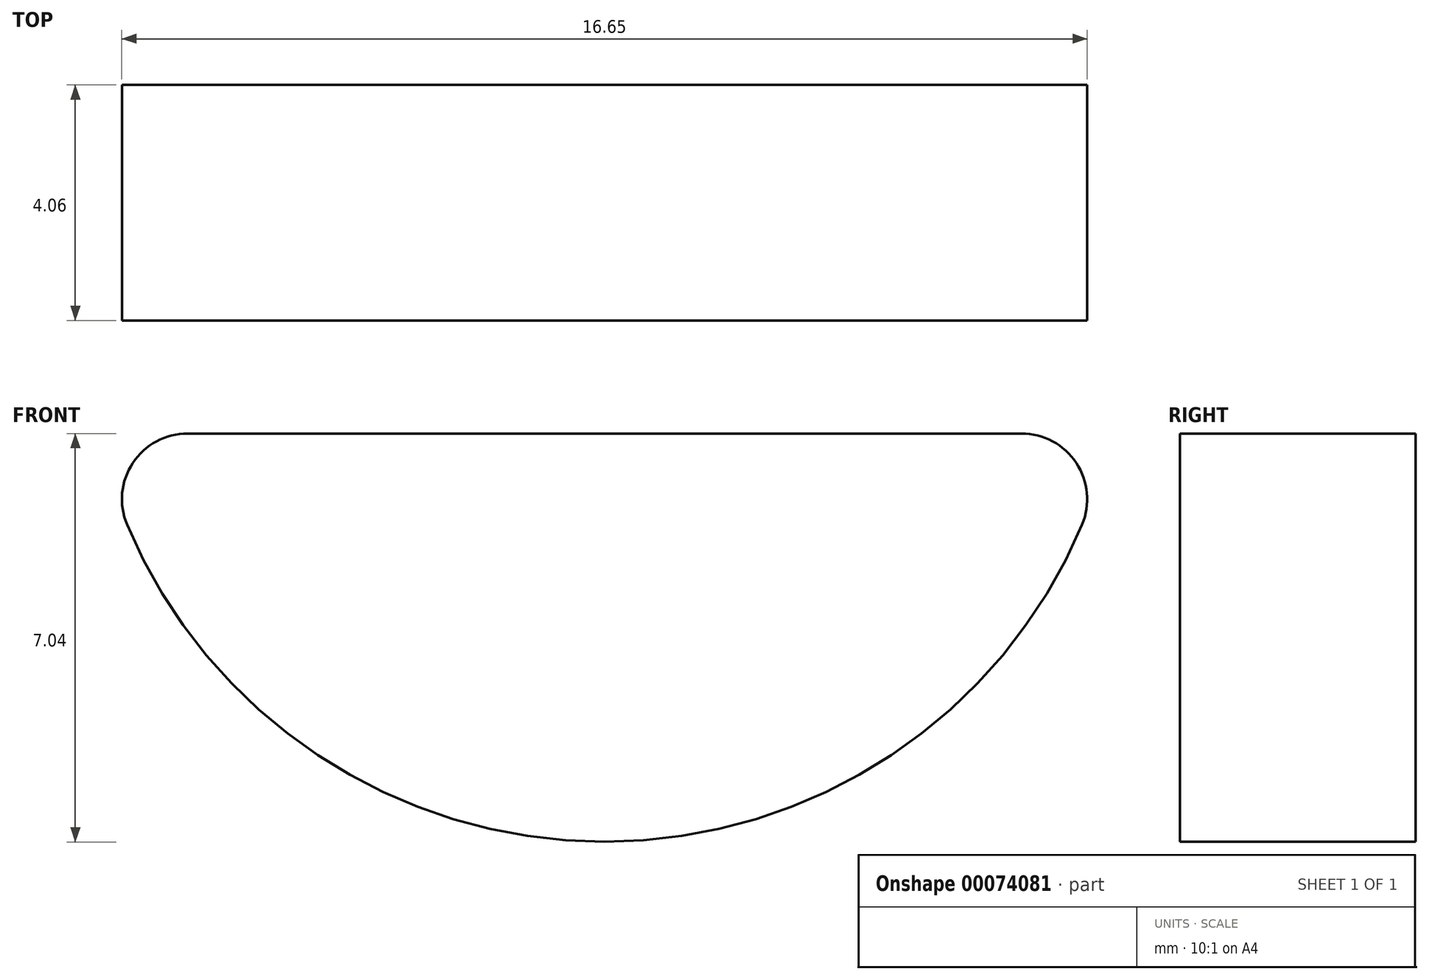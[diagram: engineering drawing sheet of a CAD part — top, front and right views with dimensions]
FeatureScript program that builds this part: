
annotation { "Feature Type Name" : "Feature", "Feature Type Description" : "" }
export const myFeature = defineFeature(function(context is Context, id is Id, definition is map)
    precondition{}
    {
        {
            var Q0;
            Q0=qCreatedBy(makeId("Front.planeOp"),FACE);
            var sketch = newSketch(context, id + "F0", { "sketchPlane" : qUnion([Q0])});
            skLineSegment(sketch, "E0", {"start": v(-8.89, 0) * mm, "end": v(8.58, 0) * mm});
            skArc(sketch, "E1", {"start": v(-8.89, 0) * mm, "mid": v(-0.15, -7.04) * mm, "end": v(8.58, 0) * mm});
            skSolve(sketch);
        }
        {
            var Q0;
            Q0=makeQuery(id+"F0.imprint","IMPRINT",FACE,{"disambiguationData":[TD([[makeQuery(id+"F0.imprint","IMPRINT",EDGE,{"derivedFrom":sQuery(id+"F0.wireOp",EDGE,"E0")}),-1.0]])]});
            extrude(context, id + "F1", {"entities" : qUnion([Q0]), "endBound" : BoundingType.SYMMETRIC, "depth" : 4.06 * mm});
        }
        {
            var Q0;
            {var subQ0=sQuery(id+"F0.wireOp",EDGE,"E1");var subQ1=sQuery(id+"F0.wireOp",EDGE,"E0");Q0=makeQuery(id+"F1.opExtrude","SWEPT_EDGE",EDGE,{"disambiguationData":[OSD([subQ1,subQ0]),TDD([makeQuery(id+"F0.imprint","INTERSECT",VERTEX,{"disambiguationData":[OD(0.0)],"derivedFrom":[subQ1,subQ0]})])]});}
            var Q1;
            {var subQ0=sQuery(id+"F0.wireOp",EDGE,"E1");var subQ1=sQuery(id+"F0.wireOp",EDGE,"E0");Q1=makeQuery(id+"F1.opExtrude","SWEPT_EDGE",EDGE,{"disambiguationData":[OSD([subQ1,subQ0]),TDD([makeQuery(id+"F0.imprint","INTERSECT",VERTEX,{"disambiguationData":[OD(1.0)],"derivedFrom":[subQ1,subQ0]})])]});}
            fillet(context, id + "F2", {"entities" : qUnion([Q0, Q1]), "radius" : 1.13 * mm, "tangentPropagation" : true, "allowEdgeOverflow" : false});
        }
    });
